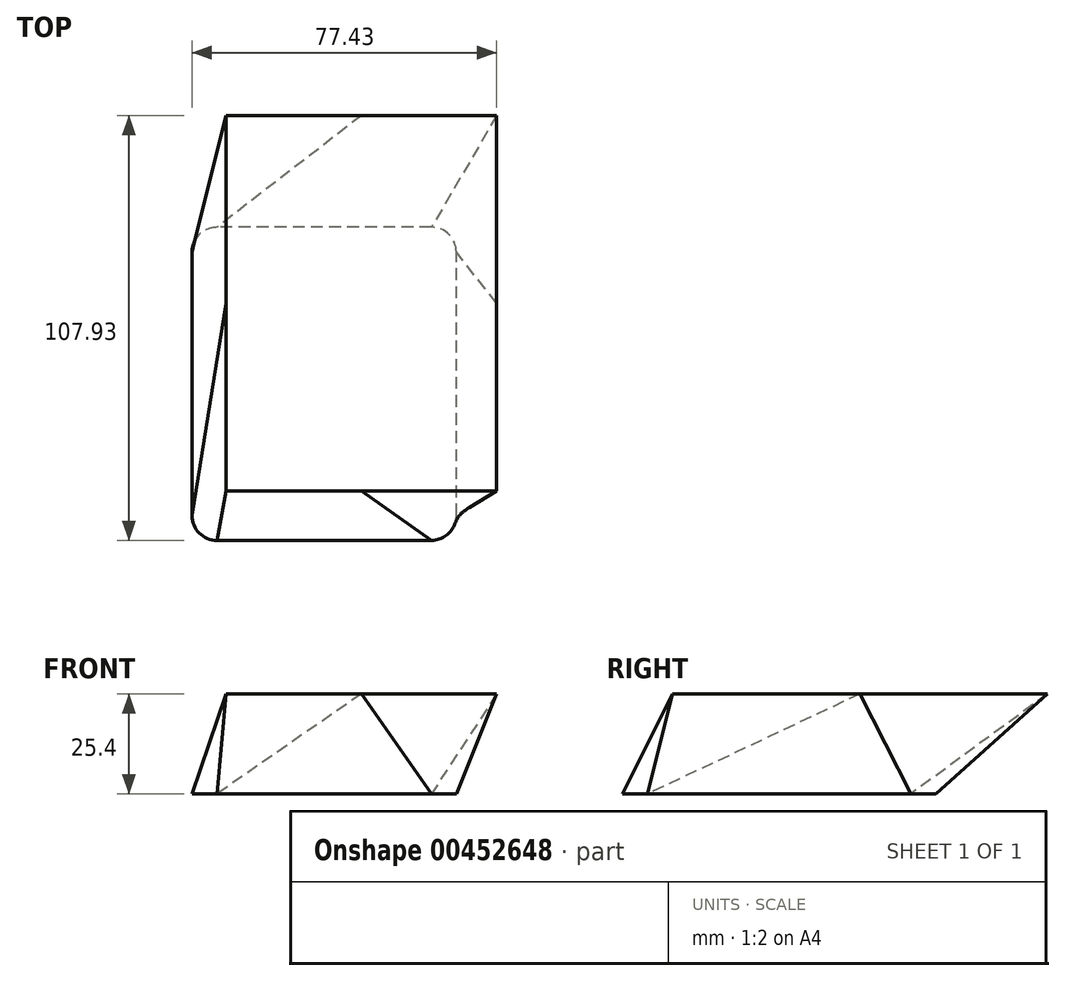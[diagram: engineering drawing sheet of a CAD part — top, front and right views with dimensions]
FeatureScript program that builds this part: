
annotation { "Feature Type Name" : "Feature", "Feature Type Description" : "" }
export const myFeature = defineFeature(function(context is Context, id is Id, definition is map)
    precondition{}
    {
        {
            var Q0;
            Q0=qCreatedBy(makeId("Top.planeOp"),FACE);
            var sketch = newSketch(context, id + "F0", { "sketchPlane" : qUnion([Q0])});
            skLineSegment(sketch, "E0.bottom", {"start": v(27.24, -39.78) * mm, "end": v(-27.24, -39.78) * mm});
            skLineSegment(sketch, "E0.top", {"start": v(27.24, 39.78) * mm, "end": v(-27.24, 39.78) * mm});
            skLineSegment(sketch, "E0.left", {"start": v(33.6, -33.43) * mm, "end": v(33.6, 33.43) * mm});
            skLineSegment(sketch, "E0.right", {"start": v(-33.6, -33.43) * mm, "end": v(-33.6, 33.43) * mm});
            skPoint(sketch, "E0.middle", {"position": v(0, 0) * mm});
            skPoint(sketch, "E1.visualSharp", {"position": v(-33.6, 39.78) * mm});
            skArc(sketch, "E1.filletArc", {"start": v(-27.24, 39.78) * mm, "mid": v(-31.73, 37.92) * mm, "end": v(-33.6, 33.43) * mm});
            skPoint(sketch, "E2.visualSharp", {"position": v(33.6, 39.78) * mm});
            skArc(sketch, "E2.filletArc", {"start": v(33.6, 33.43) * mm, "mid": v(31.73, 37.92) * mm, "end": v(27.24, 39.78) * mm});
            skPoint(sketch, "E3.visualSharp", {"position": v(33.6, -39.78) * mm});
            skArc(sketch, "E3.filletArc", {"start": v(27.24, -39.78) * mm, "mid": v(31.73, -37.92) * mm, "end": v(33.6, -33.43) * mm});
            skPoint(sketch, "E4.visualSharp", {"position": v(-33.6, -39.78) * mm});
            skArc(sketch, "E4.filletArc", {"start": v(-33.6, -33.43) * mm, "mid": v(-31.73, -37.92) * mm, "end": v(-27.24, -39.78) * mm});
            skSolve(sketch);
        }
        {
            var Q0;
            Q0=qCreatedBy(makeId("Top.planeOp"),FACE);
            cPlane(context, id + "F1", {"entities" : qUnion([Q0]), "cplaneType" : CPlaneType.OFFSET, "offset" : 25.4 * mm, "width" : 152.4 * mm, "height" : 152.4 * mm});
        }
        {
            var Q0;
            Q0=qCreatedBy(id+"F1.planeOp",FACE);
            var sketch = newSketch(context, id + "F2", { "sketchPlane" : qUnion([Q0])});
            skLineSegment(sketch, "E5.bottom", {"start": v(43.84, -27.2) * mm, "end": v(-24.94, -27.2) * mm});
            skLineSegment(sketch, "E5.top", {"start": v(43.84, 68.15) * mm, "end": v(-24.94, 68.15) * mm});
            skLineSegment(sketch, "E5.left", {"start": v(43.84, -27.2) * mm, "end": v(43.84, 68.15) * mm});
            skLineSegment(sketch, "E5.right", {"start": v(-24.94, -27.2) * mm, "end": v(-24.94, 68.15) * mm});
            skPoint(sketch, "E5.middle", {"position": v(9.45, 20.48) * mm});
            skSolve(sketch);
        }
        {
            var Q0;
            Q0=makeQuery(id+"F2.imprint","IMPRINT",FACE,{"disambiguationData":[TD([[makeQuery(id+"F2.imprint","IMPRINT",EDGE,{"derivedFrom":sQuery(id+"F2.wireOp",EDGE,"E5.bottom")}),-1.0]])]});
            var Q1;
            Q1=makeQuery(id+"F0.imprint","IMPRINT",FACE,{"disambiguationData":[TD([[makeQuery(id+"F0.imprint","IMPRINT",EDGE,{"derivedFrom":sQuery(id+"F0.wireOp",EDGE,"E0.bottom")}),-1.0]])]});
            loft(context, id + "F3", {"sheetProfilesArray" : [{ "sheetProfileEntities" : qUnion([Q0]) }, { "sheetProfileEntities" : qUnion([Q1]) }]});
        }
    });
